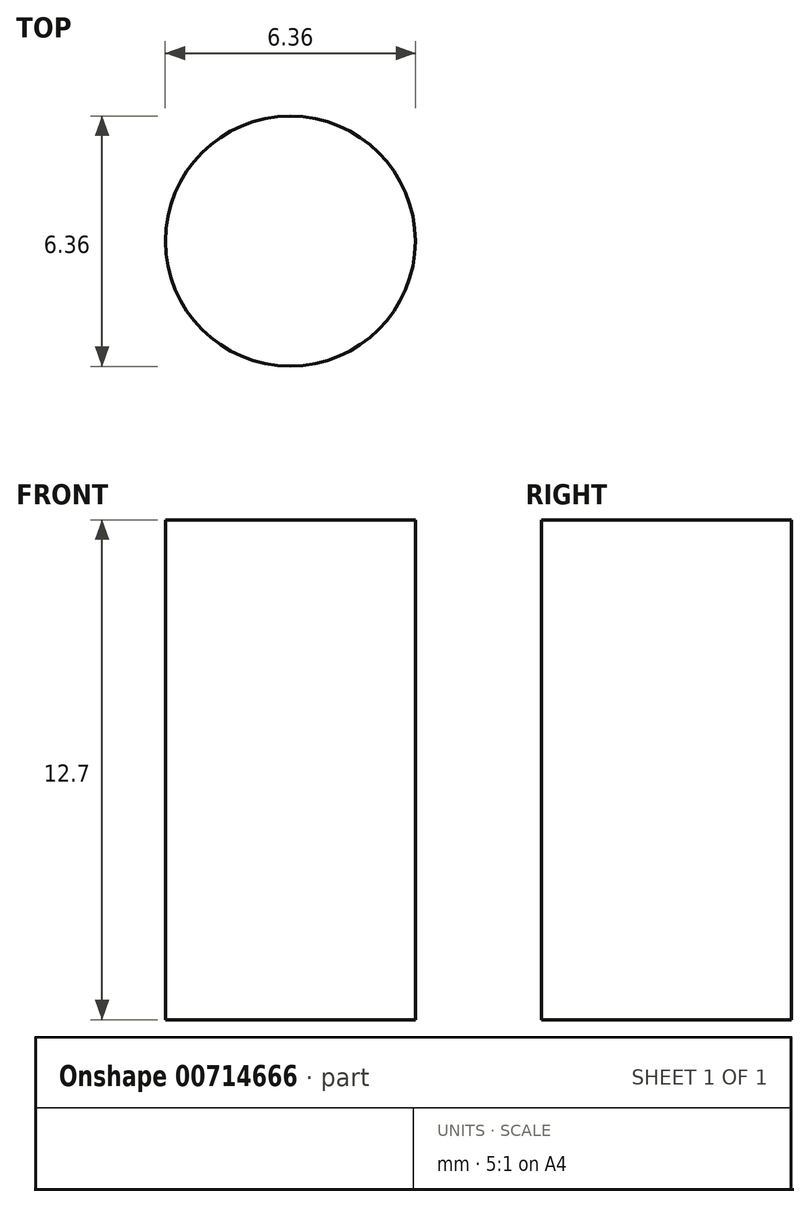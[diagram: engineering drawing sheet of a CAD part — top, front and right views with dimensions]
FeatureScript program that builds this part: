
annotation { "Feature Type Name" : "Feature", "Feature Type Description" : "" }
export const myFeature = defineFeature(function(context is Context, id is Id, definition is map)
    precondition{}
    {
        {
            var Q0;
            Q0=qCreatedBy(makeId("Top.planeOp"),FACE);
            var sketch = newSketch(context, id + "F0", { "sketchPlane" : qUnion([Q0])});
            skCircle(sketch, "E0", {"center": v(0, 0) * mm, "radius": 3.18 * mm});
            skSolve(sketch);
        }
        {
            var Q0;
            Q0=makeQuery(id+"F0.imprint","IMPRINT",FACE,{"disambiguationData":[TD([[makeQuery(id+"F0.imprint","IMPRINT",EDGE,{"derivedFrom":sQuery(id+"F0.wireOp",EDGE,"E0")}),1.0]])]});
            extrude(context, id + "F1", {"entities" : qUnion([Q0]), "depth" : 12.7 * mm, "offsetDistance" : 25.4 * mm});
        }
    });
